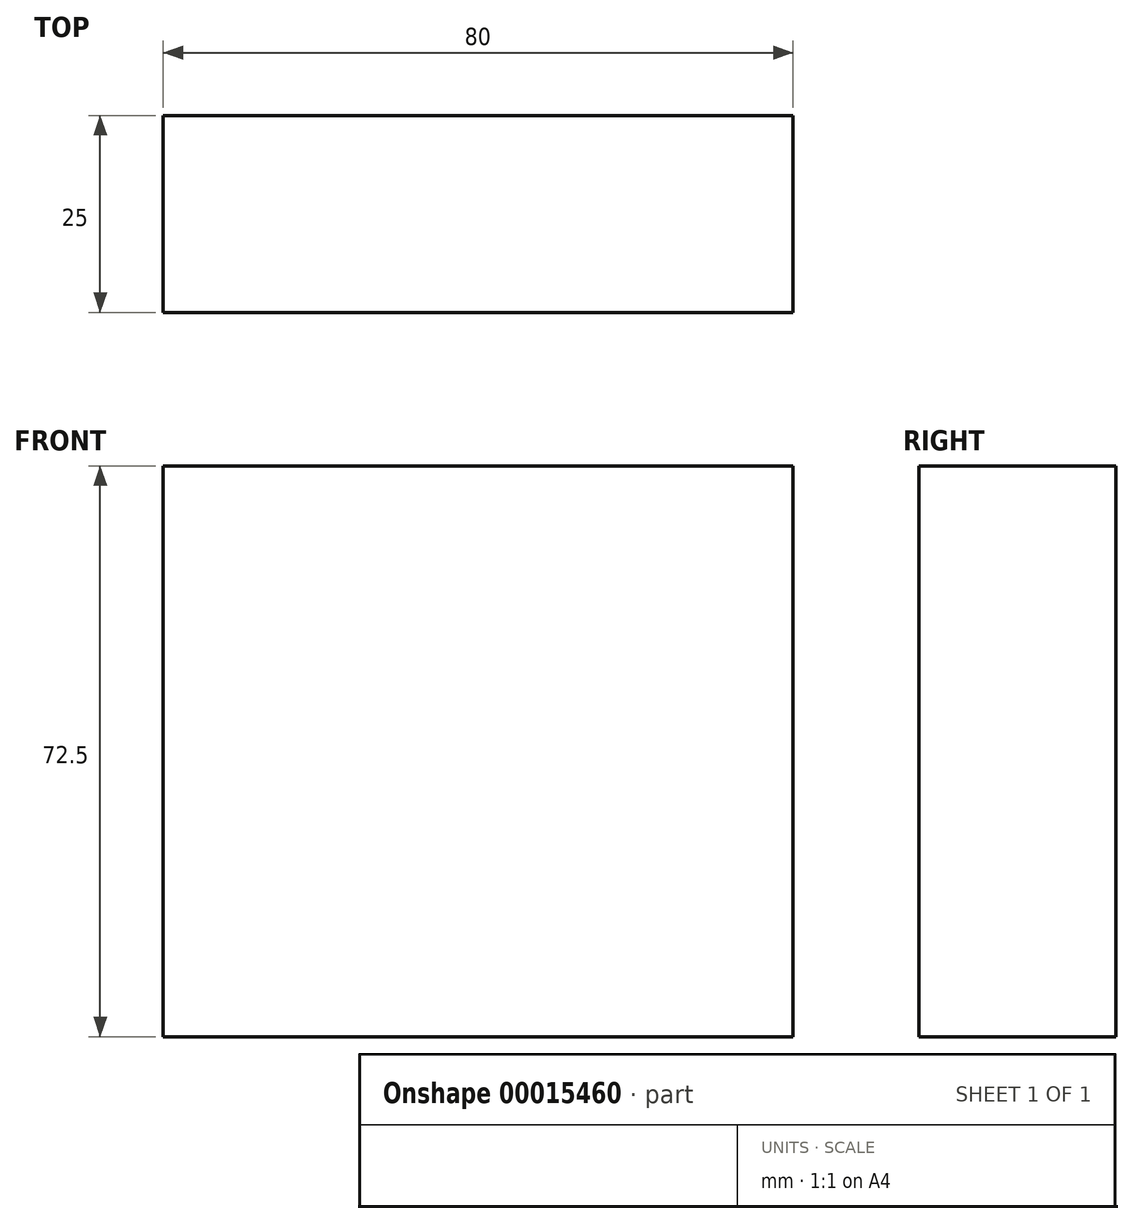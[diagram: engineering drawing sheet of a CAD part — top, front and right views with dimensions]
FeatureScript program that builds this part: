
annotation { "Feature Type Name" : "Feature", "Feature Type Description" : "" }
export const myFeature = defineFeature(function(context is Context, id is Id, definition is map)
    precondition{}
    {
        {
            var Q0;
            Q0=qCreatedBy(makeId("Front.planeOp"),FACE);
            var sketch = newSketch(context, id + "F0", { "sketchPlane" : qUnion([Q0])});
            skLineSegment(sketch, "E0.rect.bottom", {"start": v(40, -36.25) * mm, "end": v(-40, -36.25) * mm});
            skLineSegment(sketch, "E0.rect.top", {"start": v(40, 36.25) * mm, "end": v(-40, 36.25) * mm});
            skLineSegment(sketch, "E0.rect.left", {"start": v(40, -36.25) * mm, "end": v(40, 36.25) * mm});
            skLineSegment(sketch, "E0.rect.right", {"start": v(-40, -36.25) * mm, "end": v(-40, 36.25) * mm});
            skPoint(sketch, "E0.rect.middle", {"position": v(0, 0) * mm});
            skSolve(sketch);
        }
        {
            var Q0;
            Q0 = qSketchRegion(id + "F0", true);
            extrude(context, id + "F1", {"entities" : qUnion([Q0]), "depth" : 25 * mm});
        }
    });
